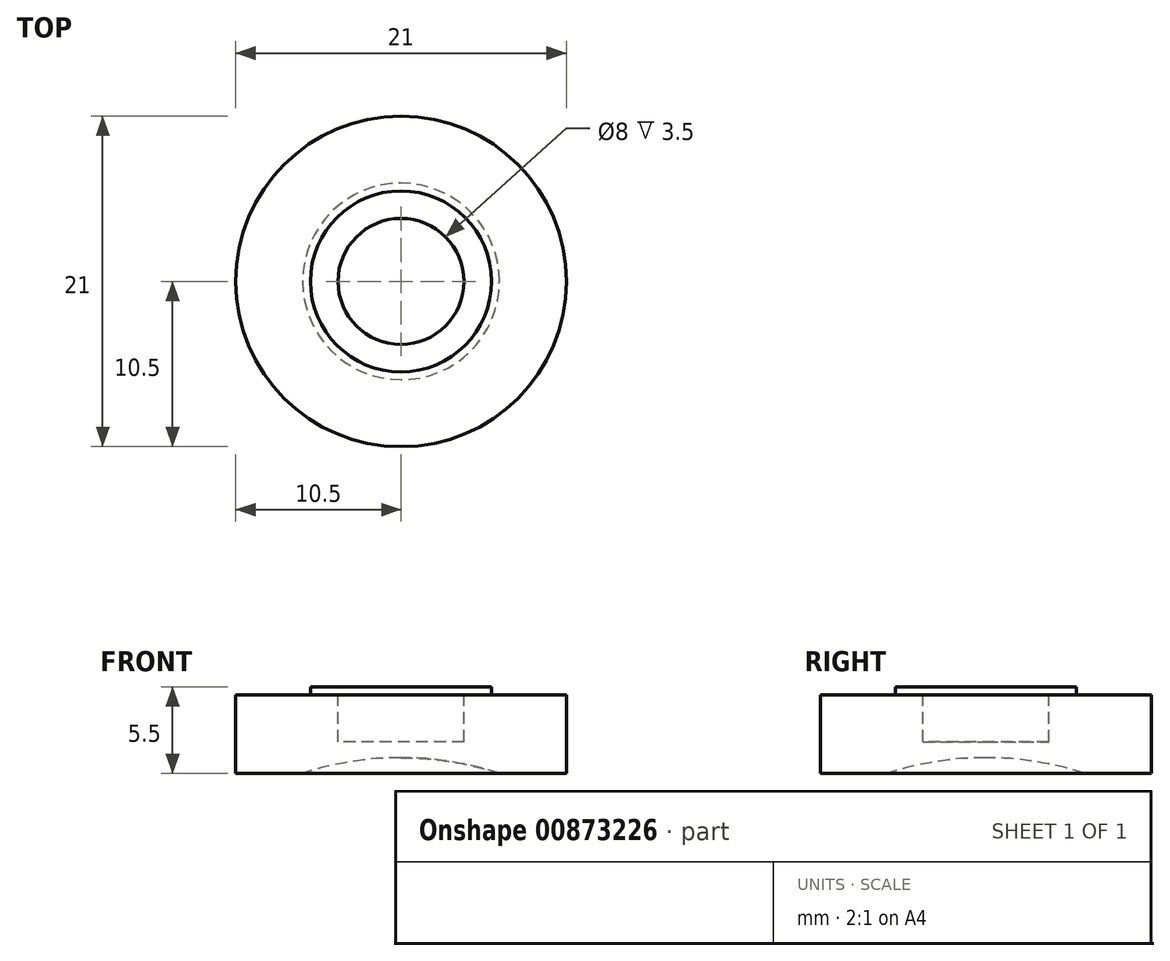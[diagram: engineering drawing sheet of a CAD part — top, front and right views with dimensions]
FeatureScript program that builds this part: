
annotation { "Feature Type Name" : "Feature", "Feature Type Description" : "" }
export const myFeature = defineFeature(function(context is Context, id is Id, definition is map)
    precondition{}
    {
        {
            var Q0;
            Q0=qCreatedBy(makeId("Top.planeOp"),FACE);
            var sketch = newSketch(context, id + "F0", { "sketchPlane" : qUnion([Q0])});
            skCircle(sketch, "E0", {"center": v(0, 0) * mm, "radius": 10.5 * mm});
            skSolve(sketch);
        }
        {
            var Q0;
            Q0 = qSketchRegion(id + "F0", true);
            extrude(context, id + "F1", {"entities" : qUnion([Q0]), "depth" : 5 * mm, "offsetDistance" : 25 * mm});
        }
        {
            var Q0;
            Q0=makeQuery(id+"F1.opExtrude","CAP_FACE",FACE,{"disambiguationData":[OSD([sQuery(id+"F0.wireOp",EDGE,"E0")])],"isStart":false});
            var sketch = newSketch(context, id + "F2", { "sketchPlane" : qUnion([Q0])});
            skCircle(sketch, "E1", {"center": v(0, 0) * mm, "radius": 5.75 * mm});
            skSolve(sketch);
        }
        {
            var Q0;
            Q0 = qSketchRegion(id + "F2", true);
            extrude(context, id + "F3", {"entities" : qUnion([Q0]), "operationType" : NewBodyOperationType.ADD, "depth" : .5 * mm, "offsetDistance" : 25 * mm});
        }
        {
            var Q0;
            Q0=makeQuery(id+"F3.opExtrude","CAP_FACE",FACE,{"disambiguationData":[OSD([sQuery(id+"F2.wireOp",EDGE,"E1")])],"isStart":false});
            var sketch = newSketch(context, id + "F4", { "sketchPlane" : qUnion([Q0])});
            skCircle(sketch, "E2", {"center": v(0, 0) * mm, "radius": 4 * mm});
            skSolve(sketch);
        }
        {
            var Q0;
            Q0 = qSketchRegion(id + "F4", true);
            extrude(context, id + "F5", {"entities" : qUnion([Q0]), "operationType" : NewBodyOperationType.REMOVE, "oppositeDirection" : true, "depth" : 3.5 * mm, "offsetDistance" : 25 * mm});
        }
        {
            var Q0;
            Q0=qCreatedBy(makeId("Front.planeOp"),FACE);
            var sketch = newSketch(context, id + "F6", { "sketchPlane" : qUnion([Q0])});
            skLineSegment(sketch, "E3.0", {"start": v(-10.5, 0) * mm, "end": v(10.5, 0) * mm, "construction": true});
            skLineSegment(sketch, "E4.0", {"start": v(-11, 1) * mm, "end": v(11, 1) * mm, "construction": true});
            skArc(sketch, "E5", {"start": v(0, -39) * mm, "mid": v(20, -19) * mm, "end": v(0, 1) * mm});
            skLineSegment(sketch, "E6", {"start": v(0, 1) * mm, "end": v(0, -39) * mm});
            skSolve(sketch);
        }
        {
            var Q0;
            Q0=makeQuery(id+"F6.imprint","IMPRINT",FACE,{"disambiguationData":[TD([[makeQuery(id+"F6.imprint","IMPRINT",EDGE,{"derivedFrom":sQuery(id+"F6.wireOp",EDGE,"E5")}),1.0]])]});
            var Q1;
            Q1=sQuery(id+"F6.wireOp",EDGE,"E6");
            revolve(context, id + "F7", {"operationType" : NewBodyOperationType.REMOVE, "surfaceOperationType" : NewSurfaceOperationType.NEW, "entities" : qUnion([Q0]), "axis" : qUnion([Q1]), "revolveType" : RevolveType.FULL, "oppositeDirection" : true});
        }
    });
